# Revit family: Power-MouldedCaseDevices-GEWISS-97MSS-CHANGE-OVER_SWITCH_3POS
name_source: partatom
category: Apparecchi elettrici
revit_build: Autodesk Revit 2016 (Build: 20161004_0715(x64)
units: mm (PartAtom-declared; Revit-internal decimal feet)

## family parameters
Condiviso = No
Host = Muro
Mantenere orientamento annotazione = Sì
Numero OmniClass = 23.80.30.00
Punto di calcolo locali = Sì
Quota connettore circolare = Usa diametro
Sempre verticale = Sì
Taglio con vuoti quando caricato = No
Tipo di parte = Normale
Titolo OmniClass = Distribution Devices

## types (1)
- GW97761 - CHANGE-OVER SWITCH I O II 4P 125A
    Catalogue = POWER
    Catalogue Range = 97 MSS
    Descrizione = CHANGE-OVER SWITCH I O II 4P 125A
    EAN code = 8011564211551
    GW - Codice Electrocod = 150
    IDF = 55d3bb61-4078-4bff-abed-4f0f13ea2eb6
    IDT = 5e6f2f36-ae44-4c4c-b281-5b61835e2b2d
    Immagine tipo = GW97761.jpg
    Modello = GW97761
    No. Chorus modules = 12
    No. of modules EN 50022 = 12
    No. of poles = 4P
    Number of poles = 4P
    Produttore = GEWISS S.p.A.
    Rated current (In) = 125A
    Rated current: = 125A
    Rated voltage = 400V
    SEO = 3 way switch
    Technical sheet = https://www.gewiss.com
    URL = https://www.gewiss.com
    Version file RFA = 18.0
